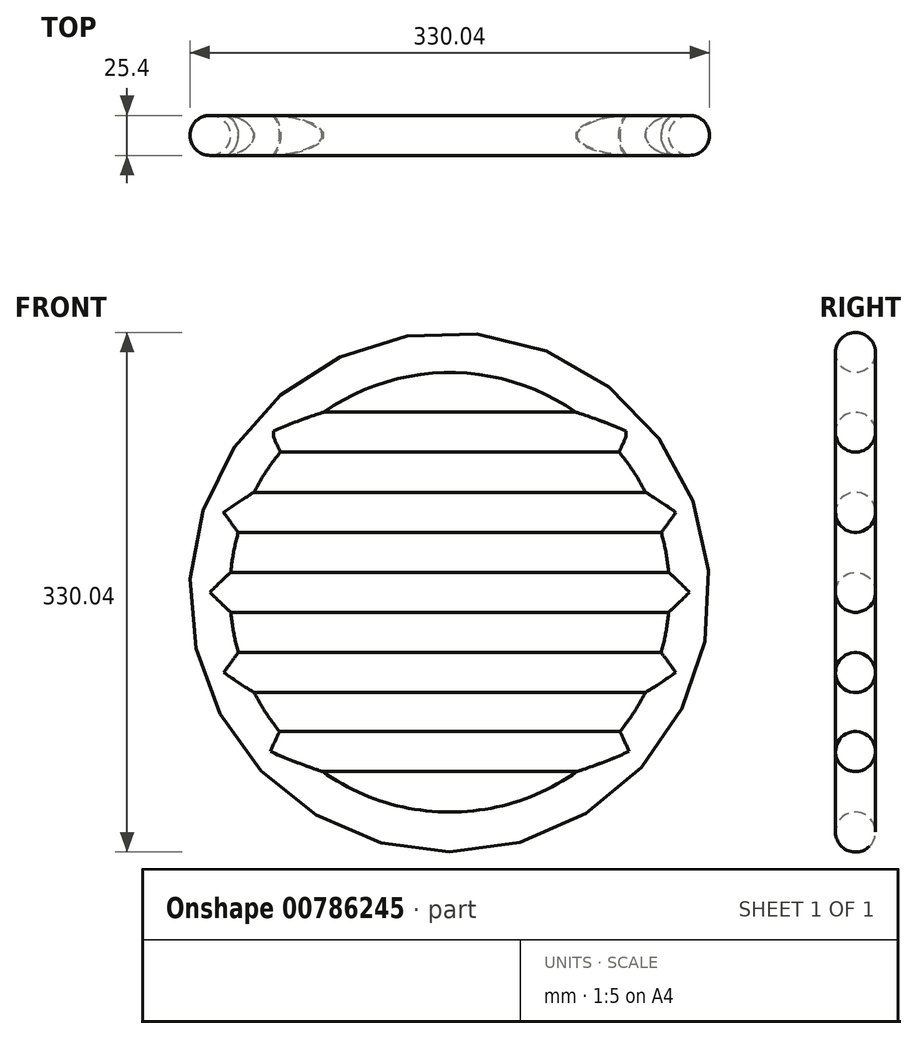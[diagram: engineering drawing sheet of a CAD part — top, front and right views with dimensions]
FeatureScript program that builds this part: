
annotation { "Feature Type Name" : "Feature", "Feature Type Description" : "" }
export const myFeature = defineFeature(function(context is Context, id is Id, definition is map)
    precondition{}
    {
        {
            var Q0;
            Q0=qCreatedBy(makeId("Front.planeOp"),FACE);
            var sketch = newSketch(context, id + "F0", { "sketchPlane" : qUnion([Q0])});
            skCircle(sketch, "E0", {"center": v(0, 0) * mm, "radius": 152.4 * mm});
            skLineSegment(sketch, "E1", {"start": v(-152.4, 0) * mm, "end": v(152.4, 0) * mm});
            skLineSegment(sketch, "E2", {"start": v(-143.68, 50.8) * mm, "end": v(143.68, 50.8) * mm});
            skLineSegment(sketch, "E3", {"start": v(-113.6, 101.6) * mm, "end": v(113.6, 101.6) * mm});
            skLineSegment(sketch, "E4", {"start": v(-143.68, -50.8) * mm, "end": v(143.68, -50.8) * mm});
            skLineSegment(sketch, "E5", {"start": v(-113.6, -101.6) * mm, "end": v(113.6, -101.6) * mm});
            skSolve(sketch);
        }
        {
            var Q0;
            Q0=qCreatedBy(makeId("Right.planeOp"),FACE);
            var sketch = newSketch(context, id + "F1", { "sketchPlane" : qUnion([Q0])});
            skCircle(sketch, "E6", {"center": v(0, 152.32) * mm, "radius": 12.7 * mm});
            skCircle(sketch, "E7", {"center": v(0, 0) * mm, "radius": 12.7 * mm});
            skCircle(sketch, "E8", {"center": v(0, 50.79) * mm, "radius": 12.7 * mm});
            skCircle(sketch, "E9", {"center": v(0, 101.77) * mm, "radius": 12.7 * mm});
            skCircle(sketch, "E10", {"center": v(0, -50.96) * mm, "radius": 12.7 * mm});
            skCircle(sketch, "E11", {"center": v(0, -101.06) * mm, "radius": 12.7 * mm});
            skSolve(sketch);
        }
        {
            var Q0;
            Q0=makeQuery(id+"F1.imprint","IMPRINT",FACE,{"disambiguationData":[TD([[makeQuery(id+"F1.imprint","IMPRINT",EDGE,{"derivedFrom":sQuery(id+"F1.wireOp",EDGE,"E6")}),1.0]])]});
            var Q1;
            Q1=sQuery(id+"F0.wireOp",EDGE,"E0");
            revolve(context, id + "F2", {"surfaceOperationType" : NewSurfaceOperationType.NEW, "entities" : qUnion([Q0]), "axis" : qUnion([Q1]), "revolveType" : RevolveType.FULL});
        }
        {
            var Q0;
            Q0=makeQuery(id+"F1.imprint","IMPRINT",FACE,{"disambiguationData":[TD([[makeQuery(id+"F1.imprint","IMPRINT",EDGE,{"derivedFrom":sQuery(id+"F1.wireOp",EDGE,"E9")}),1.0]])]});
            extrude(context, id + "F3", {"entities" : qUnion([Q0]), "operationType" : NewBodyOperationType.ADD, "endBound" : BoundingType.SYMMETRIC, "depth" : 224.03 * mm, "offsetDistance" : 25.4 * mm});
        }
        {
            var Q0;
            Q0=makeQuery(id+"F1.imprint","IMPRINT",FACE,{"disambiguationData":[TD([[makeQuery(id+"F1.imprint","IMPRINT",EDGE,{"derivedFrom":sQuery(id+"F1.wireOp",EDGE,"E8")}),1.0]])]});
            extrude(context, id + "F4", {"entities" : qUnion([Q0]), "operationType" : NewBodyOperationType.ADD, "endBound" : BoundingType.SYMMETRIC, "depth" : 287.02 * mm, "offsetDistance" : 25.4 * mm});
        }
        {
            var Q0;
            Q0=makeQuery(id+"F1.imprint","IMPRINT",FACE,{"disambiguationData":[TD([[makeQuery(id+"F1.imprint","IMPRINT",EDGE,{"derivedFrom":sQuery(id+"F1.wireOp",EDGE,"E7")}),1.0]])]});
            extrude(context, id + "F5", {"entities" : qUnion([Q0]), "operationType" : NewBodyOperationType.ADD, "endBound" : BoundingType.SYMMETRIC, "depth" : 304.65 * mm, "offsetDistance" : 25.4 * mm});
        }
        {
            var Q0;
            Q0=makeQuery(id+"F1.imprint","IMPRINT",FACE,{"disambiguationData":[TD([[makeQuery(id+"F1.imprint","IMPRINT",EDGE,{"derivedFrom":sQuery(id+"F1.wireOp",EDGE,"E10")}),1.0]])]});
            extrude(context, id + "F6", {"entities" : qUnion([Q0]), "operationType" : NewBodyOperationType.ADD, "endBound" : BoundingType.SYMMETRIC, "depth" : 287.1 * mm, "offsetDistance" : 25.4 * mm});
        }
        {
            var Q0;
            Q0=makeQuery(id+"F1.imprint","IMPRINT",FACE,{"disambiguationData":[TD([[makeQuery(id+"F1.imprint","IMPRINT",EDGE,{"derivedFrom":sQuery(id+"F1.wireOp",EDGE,"E11")}),1.0]])]});
            extrude(context, id + "F7", {"entities" : qUnion([Q0]), "operationType" : NewBodyOperationType.ADD, "endBound" : BoundingType.SYMMETRIC, "depth" : 227.93 * mm, "offsetDistance" : 25.4 * mm});
        }
        {
            var Q0;
            Q0=qCreatedBy(makeId("Top.planeOp"),FACE);
            var sketch = newSketch(context, id + "F8", { "sketchPlane" : qUnion([Q0])});
            skLineSegment(sketch, "E12.bottom", {"start": v(194.67, -63.41) * mm, "end": v(-194.67, -63.41) * mm});
            skLineSegment(sketch, "E12.top", {"start": v(194.67, 63.41) * mm, "end": v(-194.67, 63.41) * mm});
            skLineSegment(sketch, "E12.left", {"start": v(194.67, -63.41) * mm, "end": v(194.67, 63.41) * mm});
            skLineSegment(sketch, "E12.right", {"start": v(-194.67, -63.41) * mm, "end": v(-194.67, 63.41) * mm});
            skPoint(sketch, "E12.middle", {"position": v(0, 0) * mm});
            skSolve(sketch);
        }
        {
            var Q0;
            Q0=makeQuery(id+"F8.imprint","IMPRINT",FACE,{"disambiguationData":[TD([[makeQuery(id+"F8.imprint","IMPRINT",EDGE,{"derivedFrom":sQuery(id+"F8.wireOp",EDGE,"E12.bottom")}),-1.0]])]});
            var Q1;
            Q1=sQuery(id+"F8.wireOp",EDGE,"E12.right");
            var Q2;
            Q2=sQuery(id+"F8.wireOp",EDGE,"E12.bottom");
            var Q3;
            Q3=sQuery(id+"F8.wireOp",EDGE,"E12.left");
            var Q4;
            Q4=sQuery(id+"F8.wireOp",EDGE,"E12.top");
            extrude(context, id + "F9", {"entities" : qUnion([Q0]), "bodyType" : ToolBodyType.SURFACE, "surfaceEntities" : qUnion([Q1, Q2, Q3, Q4]), "endBound" : BoundingType.SYMMETRIC, "oppositeDirection" : true, "depth" : 381 * mm, "offsetDistance" : 25.4 * mm});
        }
        {
            var Q0;
            Q0=makeQuery(id+"F9.opExtrude","SWEPT_FACE",FACE,{"disambiguationData":[OSD([sQuery(id+"F8.wireOp",EDGE,"E12.bottom")])]});
            var Q1;
            Q1=makeQuery(id+"F9.opExtrude","SWEPT_FACE",FACE,{"disambiguationData":[OSD([sQuery(id+"F8.wireOp",EDGE,"E12.left")])]});
            var Q2;
            Q2=makeQuery(id+"F9.opExtrude","SWEPT_FACE",FACE,{"disambiguationData":[OSD([sQuery(id+"F8.wireOp",EDGE,"E12.top")])]});
            var Q3;
            Q3=makeQuery(id+"F9.opExtrude","SWEPT_FACE",FACE,{"disambiguationData":[OSD([sQuery(id+"F8.wireOp",EDGE,"E12.right")])]});
            fillet(context, id + "F10", {"entities" : qUnion([Q0, Q1, Q2, Q3]), "radius" : 38.1 * mm, "tangentPropagation" : true, "allowEdgeOverflow" : false});
        }
    });
